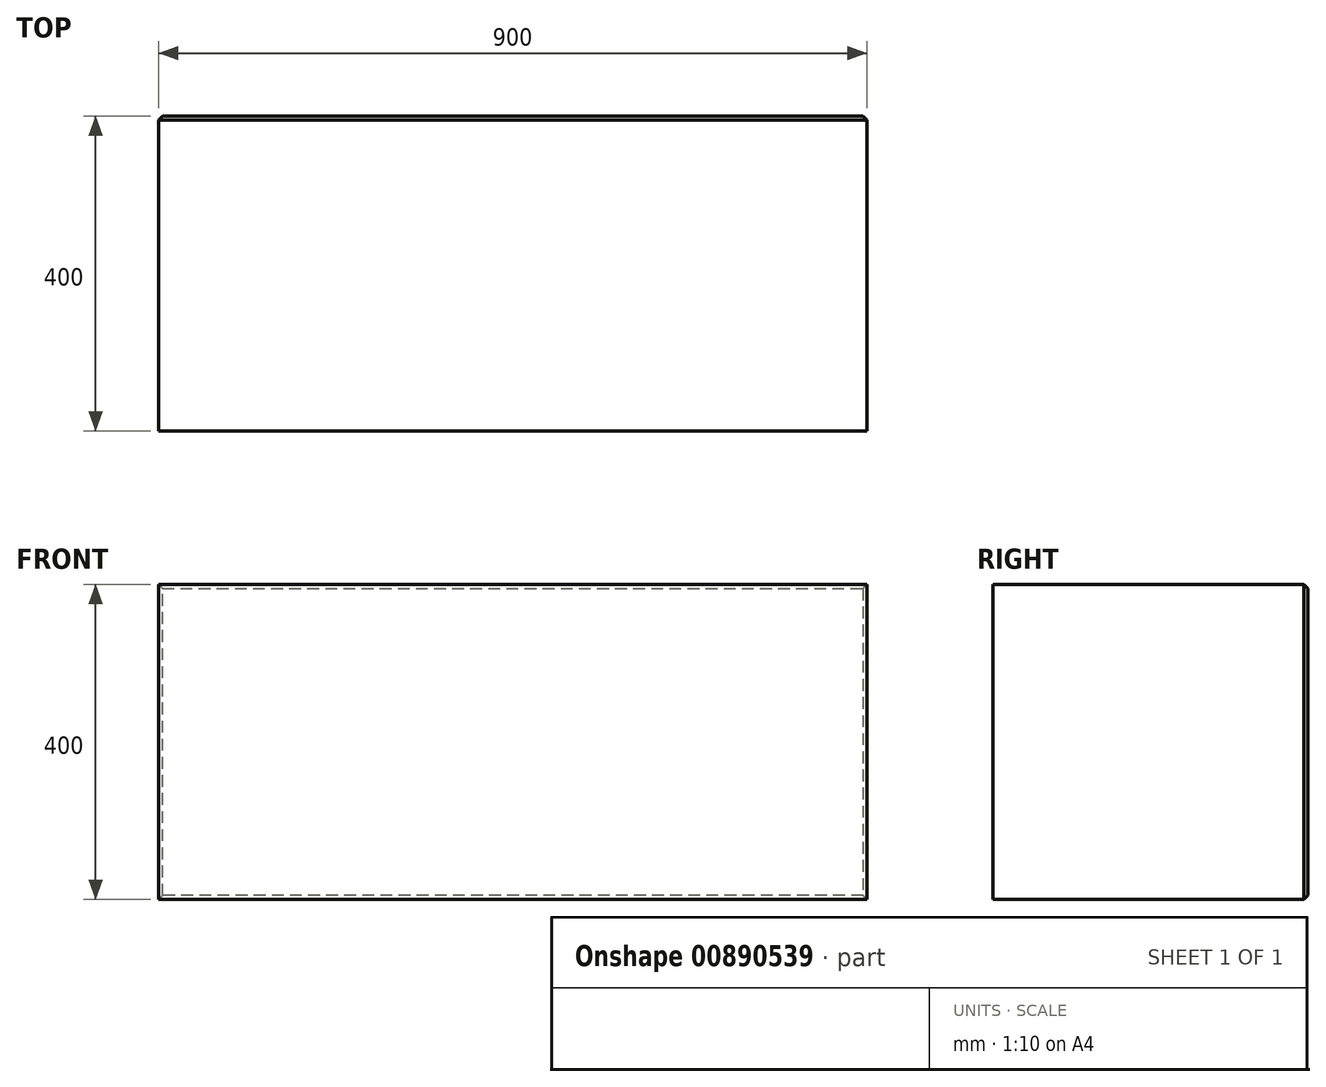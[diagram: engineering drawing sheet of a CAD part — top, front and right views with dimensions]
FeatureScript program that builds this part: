
annotation { "Feature Type Name" : "Feature", "Feature Type Description" : "" }
export const myFeature = defineFeature(function(context is Context, id is Id, definition is map)
    precondition{}
    {
        {
            var Q0;
            Q0=qCreatedBy(makeId("Front.planeOp"),FACE);
            var sketch = newSketch(context, id + "F0", { "sketchPlane" : qUnion([Q0])});
            skLineSegment(sketch, "E0.bottom", {"start": v(450, 200) * mm, "end": v(-450, 200) * mm});
            skLineSegment(sketch, "E0.top", {"start": v(450, -200) * mm, "end": v(-450, -200) * mm});
            skLineSegment(sketch, "E0.left", {"start": v(450, 200) * mm, "end": v(450, -200) * mm});
            skLineSegment(sketch, "E0.right", {"start": v(-450, 200) * mm, "end": v(-450, -200) * mm});
            skPoint(sketch, "E0.middle", {"position": v(0, 0) * mm});
            skSolve(sketch);
        }
        {
            var Q0;
            Q0=makeQuery(id+"F0.imprint","IMPRINT",FACE,{"disambiguationData":[TD([[makeQuery(id+"F0.imprint","IMPRINT",EDGE,{"derivedFrom":sQuery(id+"F0.wireOp",EDGE,"E0.bottom")}),1.0]])]});
            extrude(context, id + "F1", {"entities" : qUnion([Q0]), "depth" : 400 * mm, "offsetDistance" : 25 * mm});
        }
        {
            var Q0;
            Q0=makeQuery(id+"F1.opExtrude","CAP_FACE",FACE,{"disambiguationData":[OSD([sQuery(id+"F0.wireOp",EDGE,"E0.bottom"),sQuery(id+"F0.wireOp",EDGE,"E0.top"),sQuery(id+"F0.wireOp",EDGE,"E0.left"),sQuery(id+"F0.wireOp",EDGE,"E0.right")])],"isStart":true});
            chamfer(context, id + "F2", {"entities" : qUnion([Q0]), "width" : 5 * mm, "tangentPropagation" : true});
        }
    });
